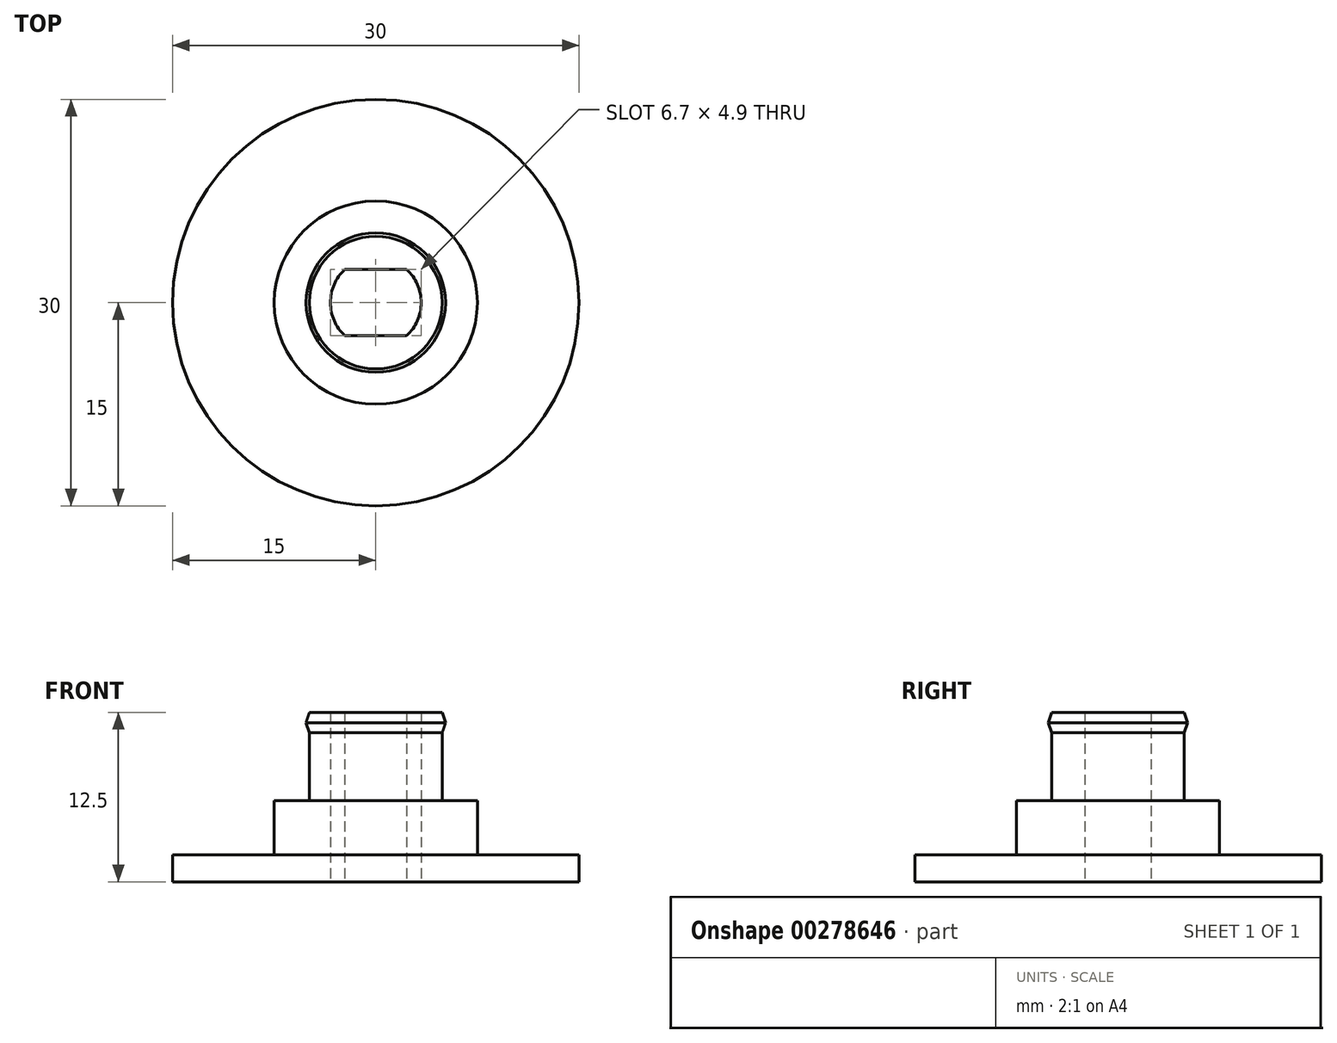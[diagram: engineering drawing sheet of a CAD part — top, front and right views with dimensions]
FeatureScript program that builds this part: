
annotation { "Feature Type Name" : "Feature", "Feature Type Description" : "" }
export const myFeature = defineFeature(function(context is Context, id is Id, definition is map)
    precondition{}
    {
        {
            assignVariable(context, id + "F0", {"name" : "e", "anyValue" : 3});
        }
        {
            assignVariable(context, id + "F1", {"name" : "h1", "anyValue" : 3});
        }
        {
            assignVariable(context, id + "F2", {"name" : "h2", "anyValue" : 6.5});
        }
        {
            var Q0;
            Q0=qCreatedBy(makeId("Top.planeOp"),FACE);
            var sketch = newSketch(context, id + "F3", { "sketchPlane" : qUnion([Q0])});
            skCircle(sketch, "E0", {"center": v(0, 0) * mm, "radius": 15 * mm});
            skCircle(sketch, "E1", {"center": v(0, 0) * mm, "radius": 7.5 * mm});
            skCircle(sketch, "E2", {"center": v(0, 0) * mm, "radius": 4.9 * mm});
            skArc(sketch, "E3", {"start": v(-2.28, 2.45) * mm, "mid": v(-3.35, 0) * mm, "end": v(-2.28, -2.45) * mm});
            skLineSegment(sketch, "E4.bottom", {"start": v(2.28, -2.45) * mm, "end": v(-2.28, -2.45) * mm});
            skLineSegment(sketch, "E4.top", {"start": v(2.28, 2.45) * mm, "end": v(-2.28, 2.45) * mm});
            skArc(sketch, "E5.trimOffspring", {"start": v(2.28, -2.45) * mm, "mid": v(3.35, 0) * mm, "end": v(2.28, 2.45) * mm});
            skPoint(sketch, "E6.orphan", {"position": v(3.35, 2.45) * mm});
            skPoint(sketch, "E7.orphan", {"position": v(3.35, -2.45) * mm});
            skPoint(sketch, "E8.orphan", {"position": v(-3.35, -2.45) * mm});
            skPoint(sketch, "E9.orphan", {"position": v(-3.35, 2.45) * mm});
            skSolve(sketch);
        }
        {
            var Q0;
            Q0=makeQuery(id+"F3.imprint","IMPRINT",FACE,{"disambiguationData":[TD([[makeQuery(id+"F3.imprint","IMPRINT",EDGE,{"derivedFrom":sQuery(id+"F3.wireOp",EDGE,"E0")}),1.0]])]});
            var Q1;
            Q1=makeQuery(id+"F3.imprint","IMPRINT",FACE,{"disambiguationData":[TD([[makeQuery(id+"F3.imprint","IMPRINT",EDGE,{"derivedFrom":sQuery(id+"F3.wireOp",EDGE,"E1")}),1.0]])]});
            var Q2;
            Q2=makeQuery(id+"F3.imprint","IMPRINT",FACE,{"disambiguationData":[TD([[makeQuery(id+"F3.imprint","IMPRINT",EDGE,{"derivedFrom":sQuery(id+"F3.wireOp",EDGE,"E2")}),1.0]])]});
            extrude(context, id + "F4", {"entities" : qUnion([Q0, Q1, Q2]), "depth" : 2 * mm});
        }
        {
            var Q0;
            Q0=makeQuery(id+"F3.imprint","IMPRINT",FACE,{"disambiguationData":[TD([[makeQuery(id+"F3.imprint","IMPRINT",EDGE,{"derivedFrom":sQuery(id+"F3.wireOp",EDGE,"E1")}),1.0]])]});
            var Q1;
            Q1=makeQuery(id+"F3.imprint","IMPRINT",FACE,{"disambiguationData":[TD([[makeQuery(id+"F3.imprint","IMPRINT",EDGE,{"derivedFrom":sQuery(id+"F3.wireOp",EDGE,"E2")}),1.0]])]});
            extrude(context, id + "F5", {"entities" : qUnion([Q0, Q1]), "operationType" : NewBodyOperationType.ADD, "depth" : (getVariable(context, 'e') + getVariable(context, 'h1')) * mm});
        }
        {
            var Q0;
            Q0=makeQuery(id+"F3.imprint","IMPRINT",FACE,{"disambiguationData":[TD([[makeQuery(id+"F3.imprint","IMPRINT",EDGE,{"derivedFrom":sQuery(id+"F3.wireOp",EDGE,"E2")}),1.0]])]});
            extrude(context, id + "F6", {"entities" : qUnion([Q0]), "operationType" : NewBodyOperationType.ADD, "depth" : (getVariable(context, 'e') + getVariable(context, 'h1') + getVariable(context, 'h2')) * mm});
        }
        {
            var Q0;
            Q0=qCreatedBy(makeId("Front.planeOp"),FACE);
            var sketch = newSketch(context, id + "F7", { "sketchPlane" : qUnion([Q0])});
            skLineSegment(sketch, "E10", {"start": v(0, 0) * mm, "end": v(0, 17.5) * mm, "construction": true});
            skLineSegment(sketch, "E11", {"start": v(-4.9, 6) * mm, "end": v(-4.9, 12.5) * mm});
            skLineSegment(sketch, "E12", {"start": v(4.9, 12.5) * mm, "end": v(4.9, 6) * mm});
            skLineSegment(sketch, "E13.bottom", {"start": v(4.9, 12.5) * mm, "end": v(5.15, 12.5) * mm, "construction": true});
            skLineSegment(sketch, "E13.top", {"start": v(4.9, 11) * mm, "end": v(5.15, 11) * mm, "construction": true});
            skLineSegment(sketch, "E13.left", {"start": v(4.9, 12.5) * mm, "end": v(4.9, 11) * mm, "construction": true});
            skLineSegment(sketch, "E13.right", {"start": v(5.15, 12.5) * mm, "end": v(5.15, 11) * mm, "construction": true});
            skPoint(sketch, "E14", {"position": v(5.15, 11.75) * mm});
            skLineSegment(sketch, "E15", {"start": v(4.9, 12.5) * mm, "end": v(5.15, 11.75) * mm});
            skLineSegment(sketch, "E16", {"start": v(5.15, 11.75) * mm, "end": v(4.9, 11) * mm});
            skLineSegment(sketch, "E17", {"start": v(4.9, 11) * mm, "end": v(4.9, 12.5) * mm});
            skSolve(sketch);
        }
        {
            var Q0;
            Q0=makeQuery(id+"F7.imprint","IMPRINT",FACE,{"disambiguationData":[TD([[makeQuery(id+"F7.imprint","IMPRINT",EDGE,{"derivedFrom":sQuery(id+"F7.wireOp",EDGE,"E15")}),-1.0]])]});
            var Q1;
            Q1=sQuery(id+"F7.wireOp",EDGE,"E10");
            revolve(context, id + "F8", {"operationType" : NewBodyOperationType.ADD, "entities" : qUnion([Q0]), "axis" : qUnion([Q1]), "revolveType" : RevolveType.FULL});
        }
        {
            var Q0;
            Q0=makeQuery(id+"F6.opExtrude","CAP_FACE",FACE,{"disambiguationData":[OSD([sQuery(id+"F3.wireOp",EDGE,"E2"),sQuery(id+"F3.wireOp",EDGE,"E3"),sQuery(id+"F3.wireOp",EDGE,"E4.bottom"),sQuery(id+"F3.wireOp",EDGE,"E4.top"),sQuery(id+"F3.wireOp",EDGE,"E5.trimOffspring")])],"isStart":false});
            cPlane(context, id + "F9", {"entities" : qUnion([Q0]), "cplaneType" : CPlaneType.OFFSET, "offset" : 0 * mm, "width" : 150 * mm, "height" : 150 * mm});
        }
    });
